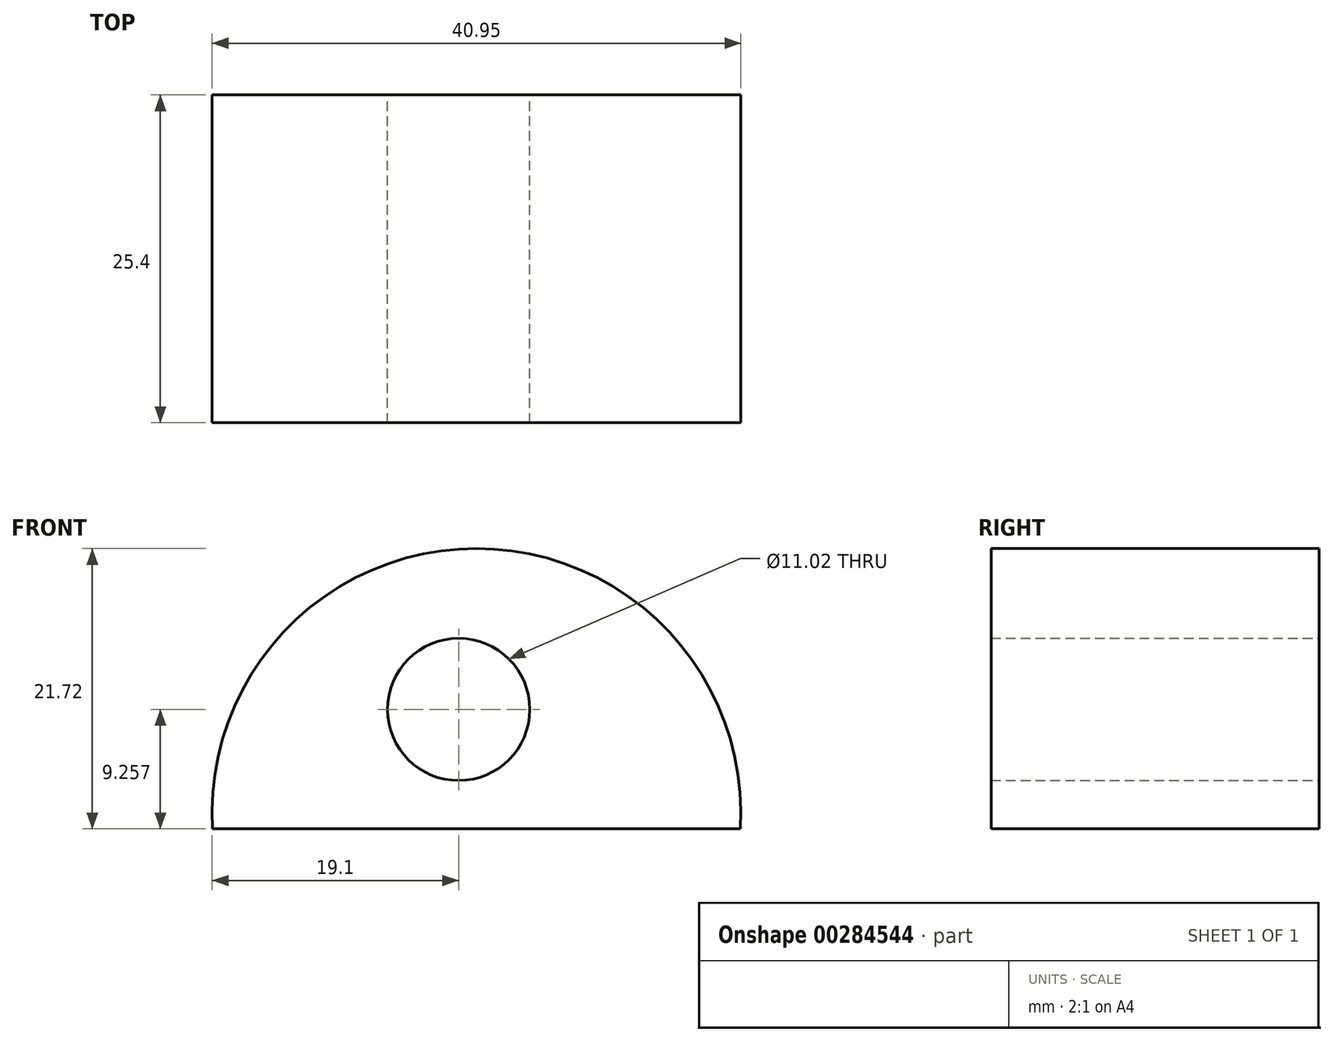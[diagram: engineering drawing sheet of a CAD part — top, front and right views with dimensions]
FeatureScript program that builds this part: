
annotation { "Feature Type Name" : "Feature", "Feature Type Description" : "" }
export const myFeature = defineFeature(function(context is Context, id is Id, definition is map)
    precondition{}
    {
        {
            var Q0;
            Q0=qCreatedBy(makeId("Front.planeOp"),FACE);
            var sketch = newSketch(context, id + "F0", { "sketchPlane" : qUnion([Q0])});
            skLineSegment(sketch, "E0", {"start": v(-19.06, 0) * mm, "end": v(21.81, 0) * mm});
            skArc(sketch, "E1", {"start": v(21.81, 0) * mm, "mid": v(1.37, 21.72) * mm, "end": v(-19.06, 0) * mm});
            skCircle(sketch, "E2", {"center": v(0, 9.26) * mm, "radius": 5.51 * mm});
            skSolve(sketch);
        }
        {
            var Q0;
            Q0=makeQuery(id+"F0.imprint","IMPRINT",FACE,{"disambiguationData":[TD([[makeQuery(id+"F0.imprint","IMPRINT",EDGE,{"derivedFrom":sQuery(id+"F0.wireOp",EDGE,"E0")}),1.0]])]});
            extrude(context, id + "F1", {"entities" : qUnion([Q0]), "depth" : 25.4 * mm});
        }
    });
